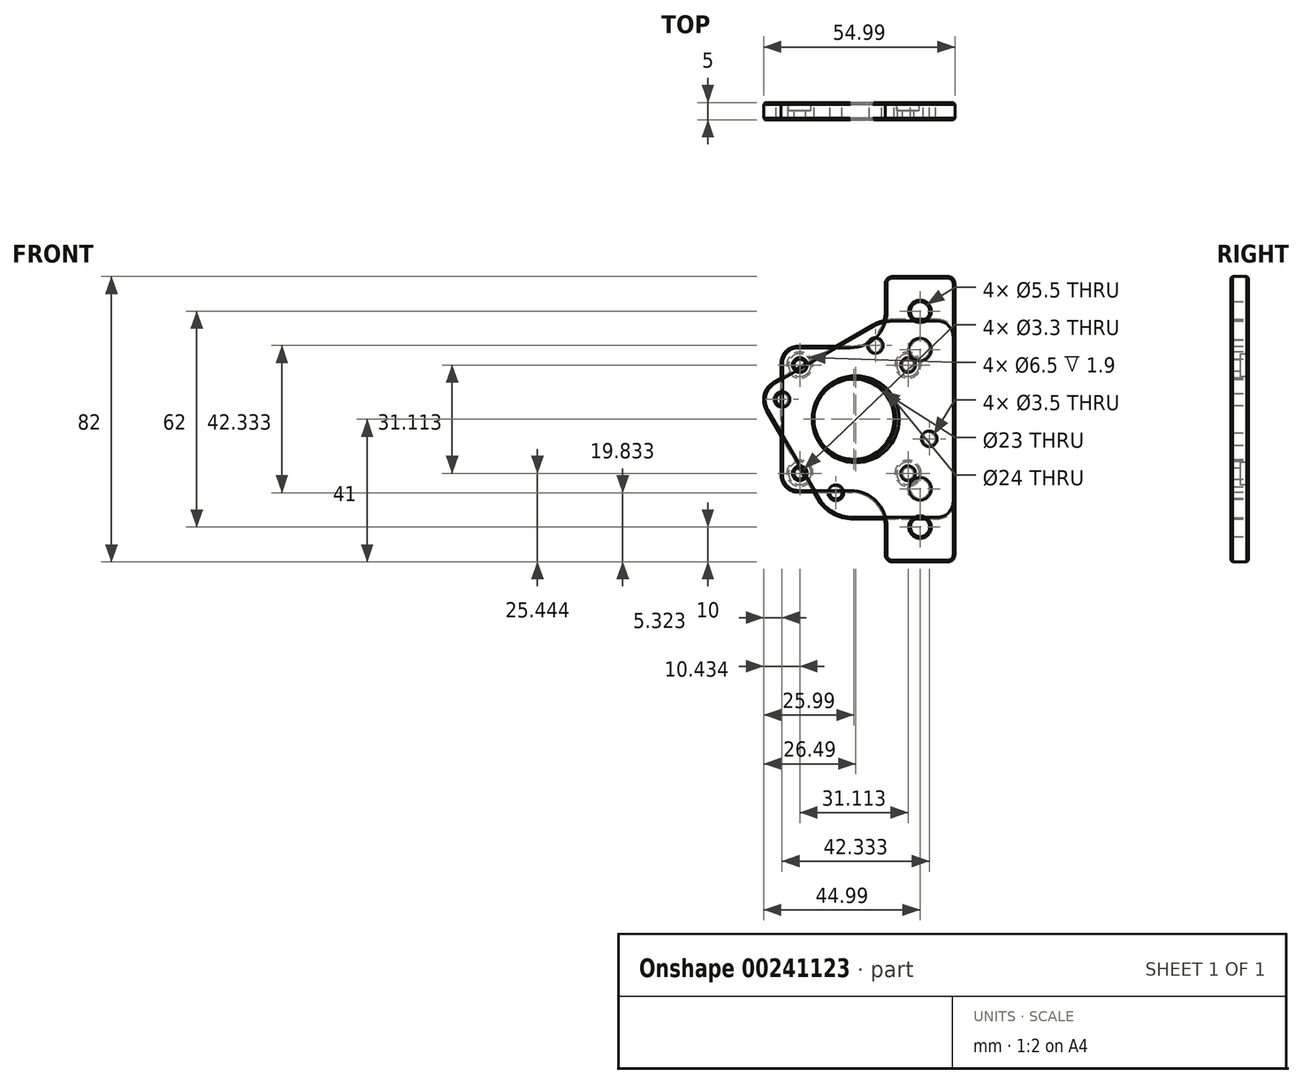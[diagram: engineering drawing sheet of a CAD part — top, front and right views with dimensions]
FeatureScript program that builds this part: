
annotation { "Feature Type Name" : "Feature", "Feature Type Description" : "" }
export const myFeature = defineFeature(function(context is Context, id is Id, definition is map)
    precondition{}
    {
        {
            var Q0;
            Q0=qCreatedBy(makeId("Front.planeOp"),FACE);
            var sketch = newSketch(context, id + "F0", { "sketchPlane" : qUnion([Q0])});
            skLineSegment(sketch, "E0.bottom", {"start": v(-0.81, 28.69) * mm, "end": v(20.19, -7.69) * mm});
            skLineSegment(sketch, "E0.top", {"start": v(-34.19, 2.5) * mm, "end": v(-19.65, -22.69) * mm});
            skLineSegment(sketch, "E0.left", {"start": v(-3.6, 27.08) * mm, "end": v(-32, 10.69) * mm});
            skLineSegment(sketch, "E0.right", {"start": v(20.19, -7.69) * mm, "end": v(-16.19, -28.69) * mm});
            skLineSegment(sketch, "E1", {"start": v(-0.81, 28.69) * mm, "end": v(-16.19, -28.69) * mm, "construction": true});
            skLineSegment(sketch, "E2", {"start": v(20.19, -7.69) * mm, "end": v(-37.19, 7.69) * mm, "construction": true});
            skCircle(sketch, "E3", {"center": v(-8.5, 0) * mm, "radius": 8.5 * mm, "construction": true});
            skLineSegment(sketch, "E4.bottom", {"start": v(-42, 21) * mm, "end": v(0, 21) * mm, "construction": true});
            skLineSegment(sketch, "E4.top", {"start": v(-42, -21) * mm, "end": v(0, -21) * mm, "construction": true});
            skLineSegment(sketch, "E4.left", {"start": v(-42, 21) * mm, "end": v(-42, -21) * mm, "construction": true});
            skLineSegment(sketch, "E4.right", {"start": v(0, 21) * mm, "end": v(0, -21) * mm, "construction": true});
            skLineSegment(sketch, "E5.bottom", {"start": v(0, 54.33) * mm, "end": v(20, 54.33) * mm, "construction": true});
            skLineSegment(sketch, "E5.top", {"start": v(0, -52.74) * mm, "end": v(20, -52.74) * mm, "construction": true});
            skLineSegment(sketch, "E5.left", {"start": v(0, 54.33) * mm, "end": v(0, -52.74) * mm, "construction": true});
            skLineSegment(sketch, "E5.right", {"start": v(20, 54.33) * mm, "end": v(20, -52.74) * mm, "construction": true});
            skLineSegment(sketch, "E6.bottom", {"start": v(7, 54.33) * mm, "end": v(13, 54.33) * mm, "construction": true});
            skLineSegment(sketch, "E6.top", {"start": v(7, -52.74) * mm, "end": v(13, -52.74) * mm, "construction": true});
            skLineSegment(sketch, "E6.left", {"start": v(7, 54.33) * mm, "end": v(7, -52.74) * mm, "construction": true});
            skLineSegment(sketch, "E6.right", {"start": v(13, 54.33) * mm, "end": v(13, -52.74) * mm, "construction": true});
            skLineSegment(sketch, "E7", {"start": v(10, 54.33) * mm, "end": v(10, -52.74) * mm, "construction": true});
            skLineSegment(sketch, "E8", {"start": v(2.4, 28.69) * mm, "end": v(20, 28.69) * mm});
            skLineSegment(sketch, "E9", {"start": v(20, 28.69) * mm, "end": v(20, -28.69) * mm});
            skLineSegment(sketch, "E10", {"start": v(20, -28.69) * mm, "end": v(-9.26, -28.69) * mm});
            skCircle(sketch, "E11", {"center": v(10, 20) * mm, "radius": 2.75 * mm});
            skCircle(sketch, "E12", {"center": v(10, -20) * mm, "radius": 2.75 * mm});
            skCircle(sketch, "E13", {"center": v(-29.67, 5.67) * mm, "radius": 1.75 * mm});
            skCircle(sketch, "E14", {"center": v(-14.17, -21.17) * mm, "radius": 1.75 * mm});
            skCircle(sketch, "E15", {"center": v(12.67, -5.67) * mm, "radius": 1.75 * mm});
            skCircle(sketch, "E16", {"center": v(-2.83, 21.17) * mm, "radius": 1.75 * mm});
            skLineSegment(sketch, "E17", {"start": v(-29.67, 5.67) * mm, "end": v(-2.83, 21.17) * mm, "construction": true});
            skLineSegment(sketch, "E18", {"start": v(-2.83, 21.17) * mm, "end": v(12.67, -5.67) * mm, "construction": true});
            skLineSegment(sketch, "E19", {"start": v(12.67, -5.67) * mm, "end": v(-14.17, -21.17) * mm, "construction": true});
            skLineSegment(sketch, "E20", {"start": v(-14.17, -21.17) * mm, "end": v(-29.67, 5.67) * mm, "construction": true});
            skPoint(sketch, "E21.visualSharp", {"position": v(-37.19, 7.69) * mm});
            skArc(sketch, "E21.filletArc", {"start": v(-32, 10.69) * mm, "mid": v(-34.79, 7.04) * mm, "end": v(-34.19, 2.5) * mm});
            skPoint(sketch, "E22.visualSharp", {"position": v(-16.19, -28.69) * mm});
            skArc(sketch, "E22.filletArc", {"start": v(-19.65, -22.69) * mm, "mid": v(-15.26, -27.08) * mm, "end": v(-9.26, -28.69) * mm});
            skPoint(sketch, "E23.visualSharp", {"position": v(-0.81, 28.69) * mm});
            skArc(sketch, "E23.filletArc", {"start": v(2.4, 28.69) * mm, "mid": v(-0.7, 28.28) * mm, "end": v(-3.6, 27.08) * mm});
            skCircle(sketch, "E24", {"center": v(-8.5, 0) * mm, "radius": 12 * mm});
            skCircle(sketch, "E25", {"center": v(10, 20) * mm, "radius": 4.5 * mm, "construction": true});
            skCircle(sketch, "E26", {"center": v(10, -20) * mm, "radius": 4.5 * mm, "construction": true});
            skSolve(sketch);
        }
        {
            var Q0;
            {var subQ7=sQuery(id+"F0.wireOp",EDGE,"E0.top");Q0=makeQuery(id+"F0.imprint","IMPRINT",FACE,{"disambiguationData":[TD([[makeQuery(id+"F0.imprint","IMPRINT",EDGE,{"derivedFrom":subQ7}),1.0]])]});}
            var Q1;
            {var subQ0=sQuery(id+"F0.wireOp",EDGE,"E8");Q1=makeQuery(id+"F0.imprint","IMPRINT",FACE,{"disambiguationData":[TD([[makeQuery(id+"F0.imprint","IMPRINT",EDGE,{"derivedFrom":subQ0}),-1.0]])]});}
            var Q2;
            {var subQ0=sQuery(id+"F0.wireOp",EDGE,"E10");Q2=makeQuery(id+"F0.imprint","IMPRINT",FACE,{"disambiguationData":[TD([[makeQuery(id+"F0.imprint","IMPRINT",EDGE,{"derivedFrom":subQ0}),-1.0]])]});}
            extrude(context, id + "F1", {"entities" : qUnion([Q0, Q1, Q2]), "depth" : 5 * mm});
        }
        {
            var Q0;
            Q0=makeQuery(id+"F1.opExtrude","SWEPT_EDGE",EDGE,{"disambiguationData":[OSD([sQuery(id+"F0.wireOp",EDGE,"E9"),sQuery(id+"F0.wireOp",EDGE,"E10")])]});
            var Q1;
            Q1=makeQuery(id+"F1.opExtrude","SWEPT_EDGE",EDGE,{"disambiguationData":[OSD([sQuery(id+"F0.wireOp",EDGE,"E8"),sQuery(id+"F0.wireOp",EDGE,"E9")])]});
            fillet(context, id + "F2", {"entities" : qUnion([Q0, Q1]), "radius" : 5 * mm, "tangentPropagation" : true, "allowEdgeOverflow" : false});
        }
        {
            var Q0;
            Q0=makeQuery(id+"F1.opExtrude","CAP_FACE",FACE,{"disambiguationData":[OSD([sQuery(id+"F0.wireOp",EDGE,"E0.top"),sQuery(id+"F0.wireOp",EDGE,"E0.left"),sQuery(id+"F0.wireOp",EDGE,"E8"),sQuery(id+"F0.wireOp",EDGE,"E9"),sQuery(id+"F0.wireOp",EDGE,"E10"),sQuery(id+"F0.wireOp",EDGE,"E11"),sQuery(id+"F0.wireOp",EDGE,"E12"),sQuery(id+"F0.wireOp",EDGE,"E13"),sQuery(id+"F0.wireOp",EDGE,"E14"),sQuery(id+"F0.wireOp",EDGE,"E15"),sQuery(id+"F0.wireOp",EDGE,"E16"),sQuery(id+"F0.wireOp",EDGE,"E21.filletArc"),sQuery(id+"F0.wireOp",EDGE,"E22.filletArc"),sQuery(id+"F0.wireOp",EDGE,"E23.filletArc"),sQuery(id+"F0.wireOp",EDGE,"E24")])],"isStart":false});
            var Q1;
            Q1=makeQuery(id+"F1.opExtrude","CAP_FACE",FACE,{"disambiguationData":[OSD([sQuery(id+"F0.wireOp",EDGE,"E0.top"),sQuery(id+"F0.wireOp",EDGE,"E0.left"),sQuery(id+"F0.wireOp",EDGE,"E8"),sQuery(id+"F0.wireOp",EDGE,"E9"),sQuery(id+"F0.wireOp",EDGE,"E10"),sQuery(id+"F0.wireOp",EDGE,"E11"),sQuery(id+"F0.wireOp",EDGE,"E12"),sQuery(id+"F0.wireOp",EDGE,"E13"),sQuery(id+"F0.wireOp",EDGE,"E14"),sQuery(id+"F0.wireOp",EDGE,"E15"),sQuery(id+"F0.wireOp",EDGE,"E16"),sQuery(id+"F0.wireOp",EDGE,"E21.filletArc"),sQuery(id+"F0.wireOp",EDGE,"E22.filletArc"),sQuery(id+"F0.wireOp",EDGE,"E23.filletArc"),sQuery(id+"F0.wireOp",EDGE,"E24")])],"isStart":true});
            chamfer(context, id + "F3", {"entities" : qUnion([Q0, Q1]), "width" : .5 * mm, "tangentPropagation" : true});
        }
        {
            var Q0;
            Q0=qCreatedBy(makeId("Front.planeOp"),FACE);
            var sketch = newSketch(context, id + "F4", { "sketchPlane" : qUnion([Q0])});
            skCircle(sketch, "E27", {"center": v(-9, 0) * mm, "radius": 9 * mm, "construction": true});
            skLineSegment(sketch, "E28", {"start": v(-30, 21) * mm, "end": v(12, -21) * mm, "construction": true});
            skLineSegment(sketch, "E29", {"start": v(-30, -21) * mm, "end": v(12, 21) * mm, "construction": true});
            skLineSegment(sketch, "E30.bottom", {"start": v(-30, 21) * mm, "end": v(12, 21) * mm, "construction": true});
            skLineSegment(sketch, "E30.top", {"start": v(-30, -21) * mm, "end": v(12, -21) * mm, "construction": true});
            skLineSegment(sketch, "E30.left", {"start": v(-30, 21) * mm, "end": v(-30, -21) * mm, "construction": true});
            skLineSegment(sketch, "E30.right", {"start": v(12, 21) * mm, "end": v(12, -21) * mm, "construction": true});
            skLineSegment(sketch, "E31.bottom", {"start": v(0, 41) * mm, "end": v(20, 41) * mm, "construction": true});
            skLineSegment(sketch, "E31.top", {"start": v(0, -41) * mm, "end": v(20, -41) * mm, "construction": true});
            skLineSegment(sketch, "E31.left", {"start": v(0, 41) * mm, "end": v(0, -41) * mm, "construction": true});
            skLineSegment(sketch, "E31.right", {"start": v(20, 41) * mm, "end": v(20, -41) * mm, "construction": true});
            skCircle(sketch, "E32", {"center": v(-9, 0) * mm, "radius": 22 * mm, "construction": true});
            skPoint(sketch, "E33", {"position": v(-24.56, 15.56) * mm});
            skPoint(sketch, "E34", {"position": v(-24.56, -15.56) * mm});
            skPoint(sketch, "E35", {"position": v(6.56, -15.56) * mm});
            skPoint(sketch, "E36", {"position": v(6.56, 15.56) * mm});
            skLineSegment(sketch, "E37", {"start": v(0, 41) * mm, "end": v(20, 21) * mm, "construction": true});
            skLineSegment(sketch, "E38", {"start": v(20, 21) * mm, "end": v(20, 41) * mm, "construction": true});
            skLineSegment(sketch, "E39", {"start": v(20, 41) * mm, "end": v(0, 21) * mm, "construction": true});
            skLineSegment(sketch, "E40", {"start": v(20, -41) * mm, "end": v(0, -21) * mm, "construction": true});
            skLineSegment(sketch, "E41", {"start": v(0, -21) * mm, "end": v(0, -41) * mm, "construction": true});
            skLineSegment(sketch, "E42", {"start": v(20, -21) * mm, "end": v(0, -41) * mm, "construction": true});
            skPoint(sketch, "E43", {"position": v(10, 31) * mm});
            skPoint(sketch, "E44", {"position": v(10, -31) * mm});
            skLineSegment(sketch, "E45", {"start": v(0, 21) * mm, "end": v(-30, 21) * mm});
            skLineSegment(sketch, "E46", {"start": v(-30, -21) * mm, "end": v(-30, 21) * mm});
            skLineSegment(sketch, "E47", {"start": v(-30, -21) * mm, "end": v(0, -21) * mm});
            skLineSegment(sketch, "E48", {"start": v(0, -21) * mm, "end": v(0, -41) * mm});
            skLineSegment(sketch, "E49", {"start": v(0, -41) * mm, "end": v(20, -41) * mm});
            skLineSegment(sketch, "E50", {"start": v(20, -41) * mm, "end": v(20, 41) * mm});
            skLineSegment(sketch, "E51", {"start": v(20, 41) * mm, "end": v(0, 41) * mm});
            skLineSegment(sketch, "E52", {"start": v(0, 41) * mm, "end": v(0, 21) * mm});
            skCircle(sketch, "E53", {"center": v(-9, 0) * mm, "radius": 11.5 * mm});
            skSolve(sketch);
        }
        {
            var Q0;
            Q0=makeQuery(id+"F4.imprint","IMPRINT",FACE,{"disambiguationData":[TD([[makeQuery(id+"F4.imprint","IMPRINT",EDGE,{"derivedFrom":sQuery(id+"F4.wireOp",EDGE,"E45")}),1.0]])]});
            extrude(context, id + "F5", {"entities" : qUnion([Q0]), "depth" : 5 * mm});
        }
        {
            var Q0;
            Q0=sQuery(id+"F4.wireOp",VERTEX,"E43");
            var Q1;
            Q1=sQuery(id+"F4.wireOp",VERTEX,"E44");
            var Q2;
            Q2=makeQuery(id+"F5.opExtrude","SWEPT_BODY",BODY,{"disambiguationData":[OSD([sQuery(id+"F4.wireOp",EDGE,"E45"),sQuery(id+"F4.wireOp",EDGE,"E46"),sQuery(id+"F4.wireOp",EDGE,"E47"),sQuery(id+"F4.wireOp",EDGE,"E48"),sQuery(id+"F4.wireOp",EDGE,"E49"),sQuery(id+"F4.wireOp",EDGE,"E50"),sQuery(id+"F4.wireOp",EDGE,"E51"),sQuery(id+"F4.wireOp",EDGE,"E52"),sQuery(id+"F4.wireOp",EDGE,"E53")])]});
            hole(context, id + "F6", {"style" : HoleStyle.SIMPLE, "endStyle" : HoleEndStyle.BLIND, "oppositeDirection" : true, "standardTappedOrClearance" : lookupTablePath({ "standard" : "ISO", "fit" : "Normal", "size" : "M5", "type" : "Clearance" }), "standardBlindInLast" : lookupTablePath({ "fit" : "Standard", "standard" : "ISO", "size" : "M5", "type" : "Clearance" }), "holeDiameter" : 5.5 * mm, "holeDepth" : 17 * mm, "tappedDepth" : 12 * mm, "tapClearance" : 3, "locations" : qUnion([Q0, Q1]), "scope" : qUnion([Q2])});
        }
        {
            var Q0;
            Q0=sQuery(id+"F4.wireOp",VERTEX,"E33");
            var Q1;
            Q1=sQuery(id+"F4.wireOp",VERTEX,"E34");
            var Q2;
            Q2=sQuery(id+"F4.wireOp",VERTEX,"E35");
            var Q3;
            Q3=sQuery(id+"F4.wireOp",VERTEX,"E36");
            var Q4;
            Q4=makeQuery(id+"F5.opExtrude","SWEPT_BODY",BODY,{"disambiguationData":[OSD([sQuery(id+"F4.wireOp",EDGE,"E45"),sQuery(id+"F4.wireOp",EDGE,"E46"),sQuery(id+"F4.wireOp",EDGE,"E47"),sQuery(id+"F4.wireOp",EDGE,"E48"),sQuery(id+"F4.wireOp",EDGE,"E49"),sQuery(id+"F4.wireOp",EDGE,"E50"),sQuery(id+"F4.wireOp",EDGE,"E51"),sQuery(id+"F4.wireOp",EDGE,"E52"),sQuery(id+"F4.wireOp",EDGE,"E53")])]});
            hole(context, id + "F7", {"style" : HoleStyle.C_BORE, "endStyle" : HoleEndStyle.BLIND, "oppositeDirection" : true, "holeDiameter" : 3.3 * mm, "cBoreDiameter" : 6.5 * mm, "cBoreDepth" : 2.4 * mm, "holeDepth" : 17 * mm, "tappedDepth" : 12 * mm, "tapClearance" : 3, "locations" : qUnion([Q0, Q1, Q2, Q3]), "scope" : qUnion([Q4])});
        }
        {
            var Q0;
            Q0=makeQuery(id+"F5.opExtrude","SWEPT_EDGE",EDGE,{"disambiguationData":[OSD([sQuery(id+"F4.wireOp",EDGE,"E47"),sQuery(id+"F4.wireOp",EDGE,"E48")])]});
            var Q1;
            Q1=makeQuery(id+"F5.opExtrude","SWEPT_EDGE",EDGE,{"disambiguationData":[OSD([sQuery(id+"F4.wireOp",EDGE,"E45"),sQuery(id+"F4.wireOp",EDGE,"E52")])]});
            fillet(context, id + "F8", {"entities" : qUnion([Q0, Q1]), "radius" : 10 * mm, "tangentPropagation" : true, "allowEdgeOverflow" : false});
        }
        {
            var Q0;
            Q0=makeQuery(id+"F5.opExtrude","SWEPT_EDGE",EDGE,{"disambiguationData":[OSD([sQuery(id+"F4.wireOp",EDGE,"E45"),sQuery(id+"F4.wireOp",EDGE,"E46")])]});
            var Q1;
            Q1=makeQuery(id+"F5.opExtrude","SWEPT_EDGE",EDGE,{"disambiguationData":[OSD([sQuery(id+"F4.wireOp",EDGE,"E46"),sQuery(id+"F4.wireOp",EDGE,"E47")])]});
            fillet(context, id + "F9", {"entities" : qUnion([Q0, Q1]), "radius" : 5 * mm, "tangentPropagation" : true, "allowEdgeOverflow" : false});
        }
        {
            var Q0;
            Q0=makeQuery(id+"F8.opFillet","BLEND_EDGE",EDGE,{"blendedFrom":[makeQuery(id+"F5.opExtrude","SWEPT_EDGE",EDGE,{"disambiguationData":[OSD([sQuery(id+"F4.wireOp",EDGE,"E45"),sQuery(id+"F4.wireOp",EDGE,"E52")])]}),makeQuery(id+"F5.opExtrude","SWEPT_FACE",FACE,{"disambiguationData":[OSD([sQuery(id+"F4.wireOp",EDGE,"E51")])]})],"blendedInto":[makeQuery(id+"F5.opExtrude","SWEPT_FACE",FACE,{"disambiguationData":[OSD([sQuery(id+"F4.wireOp",EDGE,"E51")])]})]});
            var Q1;
            Q1=makeQuery(id+"F5.opExtrude","SWEPT_EDGE",EDGE,{"disambiguationData":[OSD([sQuery(id+"F4.wireOp",EDGE,"E50"),sQuery(id+"F4.wireOp",EDGE,"E51")])]});
            var Q2;
            Q2=makeQuery(id+"F8.opFillet","BLEND_EDGE",EDGE,{"blendedFrom":[makeQuery(id+"F5.opExtrude","SWEPT_EDGE",EDGE,{"disambiguationData":[OSD([sQuery(id+"F4.wireOp",EDGE,"E47"),sQuery(id+"F4.wireOp",EDGE,"E48")])]}),makeQuery(id+"F5.opExtrude","SWEPT_FACE",FACE,{"disambiguationData":[OSD([sQuery(id+"F4.wireOp",EDGE,"E49")])]})],"blendedInto":[makeQuery(id+"F5.opExtrude","SWEPT_FACE",FACE,{"disambiguationData":[OSD([sQuery(id+"F4.wireOp",EDGE,"E49")])]})]});
            var Q3;
            Q3=makeQuery(id+"F5.opExtrude","SWEPT_EDGE",EDGE,{"disambiguationData":[OSD([sQuery(id+"F4.wireOp",EDGE,"E49"),sQuery(id+"F4.wireOp",EDGE,"E50")])]});
            var Q4;
            Q4=makeQuery(id+"F5.opExtrude","SWEPT_EDGE",EDGE,{"disambiguationData":[OSD([sQuery(id+"F4.wireOp",EDGE,"E51"),sQuery(id+"F4.wireOp",EDGE,"E52")])]});
            var Q5;
            Q5=makeQuery(id+"F5.opExtrude","SWEPT_EDGE",EDGE,{"disambiguationData":[OSD([sQuery(id+"F4.wireOp",EDGE,"E48"),sQuery(id+"F4.wireOp",EDGE,"E49")])]});
            fillet(context, id + "F10", {"entities" : qUnion([Q0, Q1, Q2, Q3, Q4, Q5]), "radius" : 2 * mm, "tangentPropagation" : true, "allowEdgeOverflow" : false});
        }
        {
            var Q0;
            Q0=makeQuery(id+"F5.opExtrude","CAP_FACE",FACE,{"disambiguationData":[OSD([sQuery(id+"F4.wireOp",EDGE,"E45"),sQuery(id+"F4.wireOp",EDGE,"E46"),sQuery(id+"F4.wireOp",EDGE,"E47"),sQuery(id+"F4.wireOp",EDGE,"E48"),sQuery(id+"F4.wireOp",EDGE,"E49"),sQuery(id+"F4.wireOp",EDGE,"E50"),sQuery(id+"F4.wireOp",EDGE,"E51"),sQuery(id+"F4.wireOp",EDGE,"E52"),sQuery(id+"F4.wireOp",EDGE,"E53")])],"isStart":false});
            var Q1;
            Q1=makeQuery(id+"F5.opExtrude","CAP_FACE",FACE,{"disambiguationData":[OSD([sQuery(id+"F4.wireOp",EDGE,"E45"),sQuery(id+"F4.wireOp",EDGE,"E46"),sQuery(id+"F4.wireOp",EDGE,"E47"),sQuery(id+"F4.wireOp",EDGE,"E48"),sQuery(id+"F4.wireOp",EDGE,"E49"),sQuery(id+"F4.wireOp",EDGE,"E50"),sQuery(id+"F4.wireOp",EDGE,"E51"),sQuery(id+"F4.wireOp",EDGE,"E52"),sQuery(id+"F4.wireOp",EDGE,"E53")])],"isStart":true});
            chamfer(context, id + "F11", {"entities" : qUnion([Q0, Q1]), "width" : .5 * mm, "tangentPropagation" : true});
        }
    });
